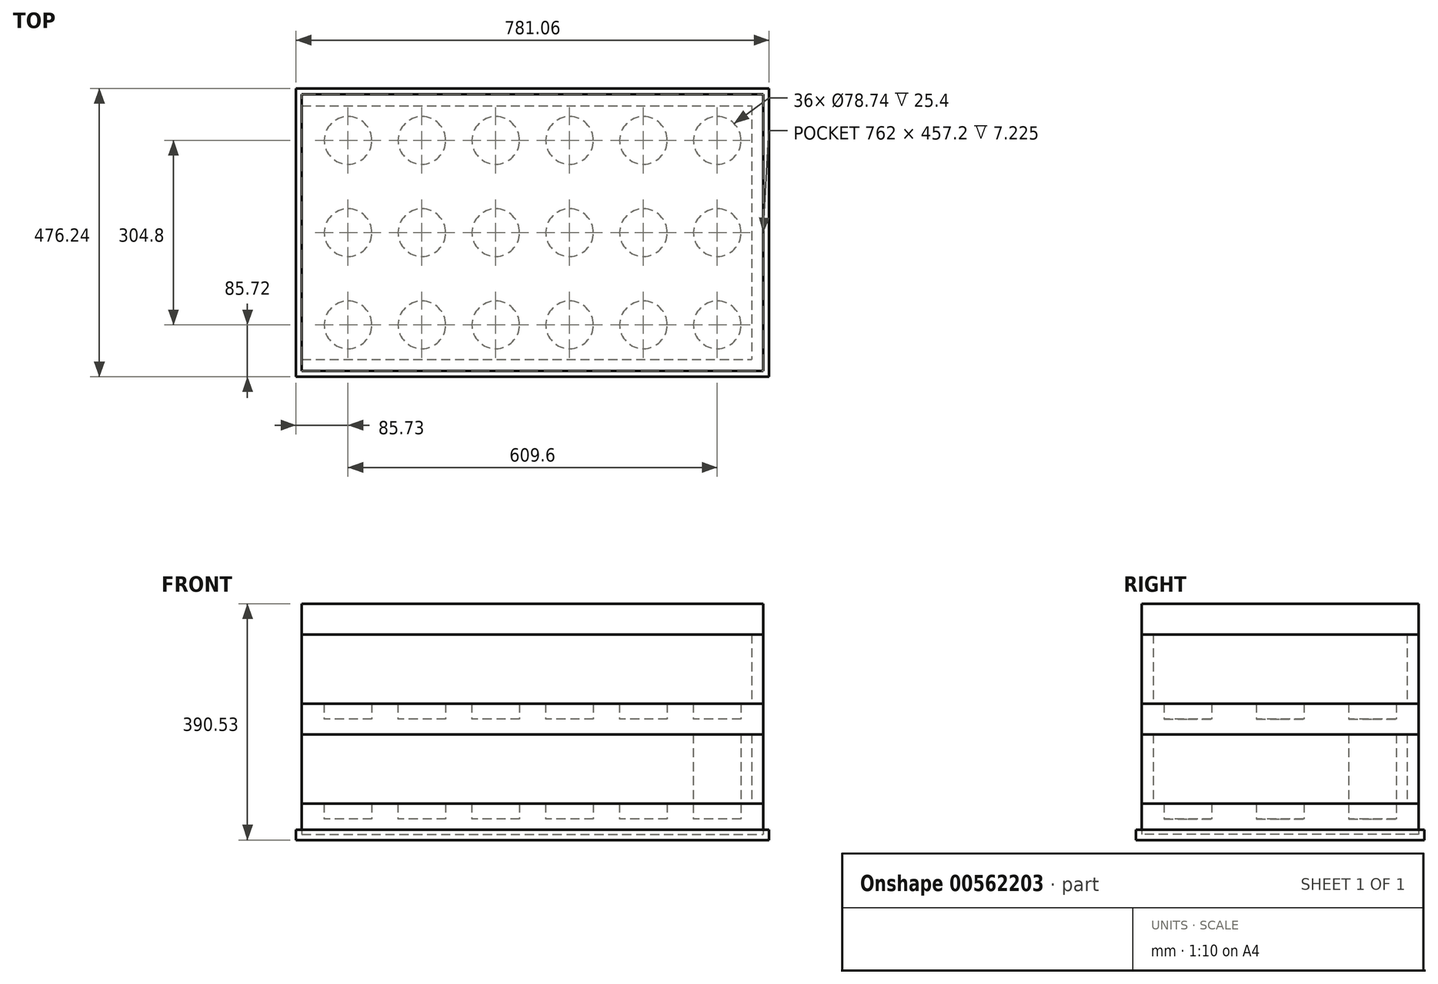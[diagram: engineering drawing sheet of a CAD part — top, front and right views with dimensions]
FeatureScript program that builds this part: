
annotation { "Feature Type Name" : "Feature", "Feature Type Description" : "" }
export const myFeature = defineFeature(function(context is Context, id is Id, definition is map)
    precondition{}
    {
        {
            var Q0;
            Q0=qCreatedBy(makeId("Top.planeOp"),FACE);
            var sketch = newSketch(context, id + "F0", { "sketchPlane" : qUnion([Q0])});
            skLineSegment(sketch, "E0.bottom", {"start": v(-390.53, 238.13) * mm, "end": v(390.53, 238.13) * mm});
            skLineSegment(sketch, "E0.top", {"start": v(-390.53, -238.13) * mm, "end": v(390.53, -238.13) * mm});
            skLineSegment(sketch, "E0.left", {"start": v(-390.53, 238.13) * mm, "end": v(-390.53, -238.13) * mm});
            skLineSegment(sketch, "E0.right", {"start": v(390.53, 238.13) * mm, "end": v(390.52, -238.12) * mm});
            skLineSegment(sketch, "E1", {"start": v(-390.53, 0) * mm, "end": v(390.53, 0) * mm, "construction": true});
            skLineSegment(sketch, "E2", {"start": v(0, -238.13) * mm, "end": v(0, 238.13) * mm, "construction": true});
            skSolve(sketch);
        }
        {
            var Q0;
            Q0=makeQuery(id+"F0.imprint","IMPRINT",FACE,{"disambiguationData":[TD([[makeQuery(id+"F0.imprint","IMPRINT",EDGE,{"derivedFrom":sQuery(id+"F0.wireOp",EDGE,"E0.bottom")}),-1.0]])]});
            extrude(context, id + "F1", {"entities" : qUnion([Q0]), "depth" : (16 + (3 / 8) * 2) * mm, "offsetDistance" : 25.4 * mm});
        }
        {
            var Q0;
            Q0=makeQuery(id+"F1.opExtrude","CAP_FACE",FACE,{"disambiguationData":[OSD([sQuery(id+"F0.wireOp",EDGE,"E0.bottom"),sQuery(id+"F0.wireOp",EDGE,"E0.top"),sQuery(id+"F0.wireOp",EDGE,"E0.left"),sQuery(id+"F0.wireOp",EDGE,"E0.right")])],"isStart":false});
            shell(context, id + "F2", {"entities" : qUnion([Q0]), "thickness" : 9.52 * mm});
        }
        {
            var Q0;
            Q0=makeQuery(id+"F2.opShell","OFFSET_FACE",FACE,{"disambiguationData":[OSD([sQuery(id+"F0.wireOp",EDGE,"E0.bottom"),sQuery(id+"F0.wireOp",EDGE,"E0.top"),sQuery(id+"F0.wireOp",EDGE,"E0.left"),sQuery(id+"F0.wireOp",EDGE,"E0.right")])]});
            var sketch = newSketch(context, id + "F3", { "sketchPlane" : qUnion([Q0])});
            skLineSegment(sketch, "E3.bottom", {"start": v(381, 228.6) * mm, "end": v(-381, 228.6) * mm});
            skLineSegment(sketch, "E3.top", {"start": v(381, -228.6) * mm, "end": v(-381, -228.6) * mm});
            skLineSegment(sketch, "E3.left", {"start": v(381, 228.6) * mm, "end": v(381, -228.6) * mm});
            skLineSegment(sketch, "E3.right", {"start": v(-381, 228.6) * mm, "end": v(-381, -228.6) * mm});
            skSolve(sketch);
        }
        {
            var Q0;
            Q0=makeQuery(id+"F3.imprint","IMPRINT",FACE,{"disambiguationData":[TD([[makeQuery(id+"F3.imprint","IMPRINT",EDGE,{"derivedFrom":sQuery(id+"F3.wireOp",EDGE,"E3.bottom")}),-1.0]])]});
            extrude(context, id + "F4", {"entities" : qUnion([Q0]), "depth" : 25.4 * mm, "offsetDistance" : 25.4 * mm});
        }
        {
            var Q0;
            Q0=makeQuery(id+"F4.opExtrude","CAP_FACE",FACE,{"disambiguationData":[OSD([sQuery(id+"F3.wireOp",EDGE,"E3.bottom"),sQuery(id+"F3.wireOp",EDGE,"E3.top"),sQuery(id+"F3.wireOp",EDGE,"E3.left"),sQuery(id+"F3.wireOp",EDGE,"E3.right")])],"isStart":false});
            var sketch = newSketch(context, id + "F5", { "sketchPlane" : qUnion([Q0])});
            skCircle(sketch, "E4", {"center": v(304.8, 152.4) * mm, "radius": 39.37 * mm});
            skCircle(sketch, "E5.0.1.0", {"center": v(304.8, 0) * mm, "radius": 39.37 * mm});
            skCircle(sketch, "E5.0.2.0", {"center": v(304.8, -152.4) * mm, "radius": 39.37 * mm});
            skCircle(sketch, "E5.1.0.0", {"center": v(182.88, 152.4) * mm, "radius": 39.37 * mm});
            skCircle(sketch, "E5.1.1.0", {"center": v(182.88, 0) * mm, "radius": 39.37 * mm});
            skCircle(sketch, "E5.1.2.0", {"center": v(182.88, -152.4) * mm, "radius": 39.37 * mm});
            skCircle(sketch, "E5.2.0.0", {"center": v(60.96, 152.4) * mm, "radius": 39.37 * mm});
            skCircle(sketch, "E5.2.1.0", {"center": v(60.96, 0) * mm, "radius": 39.37 * mm});
            skCircle(sketch, "E5.2.2.0", {"center": v(60.96, -152.4) * mm, "radius": 39.37 * mm});
            skCircle(sketch, "E5.3.0.0", {"center": v(-60.96, 152.4) * mm, "radius": 39.37 * mm});
            skCircle(sketch, "E5.3.1.0", {"center": v(-60.96, 0) * mm, "radius": 39.37 * mm});
            skCircle(sketch, "E5.3.2.0", {"center": v(-60.96, -152.4) * mm, "radius": 39.37 * mm});
            skCircle(sketch, "E5.4.0.0", {"center": v(-182.88, 152.4) * mm, "radius": 39.37 * mm});
            skCircle(sketch, "E5.4.1.0", {"center": v(-182.88, 0) * mm, "radius": 39.37 * mm});
            skCircle(sketch, "E5.4.2.0", {"center": v(-182.88, -152.4) * mm, "radius": 39.37 * mm});
            skCircle(sketch, "E5.5.0.0", {"center": v(-304.8, 152.4) * mm, "radius": 39.37 * mm});
            skCircle(sketch, "E5.5.1.0", {"center": v(-304.8, 0) * mm, "radius": 39.37 * mm});
            skCircle(sketch, "E5.5.2.0", {"center": v(-304.8, -152.4) * mm, "radius": 39.37 * mm});
            skLineSegment(sketch, "E5.direction1", {"start": v(304.8, 152.4) * mm, "end": v(182.88, 152.4) * mm, "construction": true});
            skLineSegment(sketch, "E5.direction2", {"start": v(304.8, 152.4) * mm, "end": v(304.8, 0) * mm, "construction": true});
            skSolve(sketch);
        }
        {
            var Q0;
            Q0=makeQuery(id+"F5.imprint","IMPRINT",FACE,{"disambiguationData":[TD([[makeQuery(id+"F5.imprint","IMPRINT",EDGE,{"derivedFrom":sQuery(id+"F5.wireOp",EDGE,"E4")}),-1.0]])]});
            extrude(context, id + "F6", {"entities" : qUnion([Q0]), "operationType" : NewBodyOperationType.ADD, "depth" : 25.4 * mm, "offsetDistance" : 25.4 * mm});
        }
        {
            var Q0;
            Q0=makeQuery(id+"F6.boolean.opBoolean","SPLIT",FACE,{"disambiguationData":[TD([makeQuery(id+"F6.opExtrude","SWEPT_FACE",FACE,{"disambiguationData":[OSD([sQuery(id+"F5.wireOp",EDGE,"E4")])]})])],"derivedFrom":makeQuery(id+"F4.opExtrude","CAP_FACE",FACE,{"disambiguationData":[OSD([sQuery(id+"F3.wireOp",EDGE,"E3.bottom"),sQuery(id+"F3.wireOp",EDGE,"E3.top"),sQuery(id+"F3.wireOp",EDGE,"E3.left"),sQuery(id+"F3.wireOp",EDGE,"E3.right")])],"isStart":false})});
            extrude(context, id + "F7", {"entities" : qUnion([Q0]), "depth" : 139.7 * mm, "offsetDistance" : 25.4 * mm});
        }
        {
            var Q0;
            Q0=makeQuery(id+"F6.opExtrude","CAP_FACE",FACE,{"disambiguationData":[OSD([sQuery(id+"F3.wireOp",EDGE,"E3.bottom"),sQuery(id+"F3.wireOp",EDGE,"E3.top"),sQuery(id+"F3.wireOp",EDGE,"E3.left"),sQuery(id+"F3.wireOp",EDGE,"E3.right"),sQuery(id+"F5.wireOp",EDGE,"E4"),sQuery(id+"F5.wireOp",EDGE,"E5.0.1.0"),sQuery(id+"F5.wireOp",EDGE,"E5.0.2.0"),sQuery(id+"F5.wireOp",EDGE,"E5.1.0.0"),sQuery(id+"F5.wireOp",EDGE,"E5.1.1.0"),sQuery(id+"F5.wireOp",EDGE,"E5.1.2.0"),sQuery(id+"F5.wireOp",EDGE,"E5.2.0.0"),sQuery(id+"F5.wireOp",EDGE,"E5.2.1.0"),sQuery(id+"F5.wireOp",EDGE,"E5.2.2.0"),sQuery(id+"F5.wireOp",EDGE,"E5.3.0.0"),sQuery(id+"F5.wireOp",EDGE,"E5.3.1.0"),sQuery(id+"F5.wireOp",EDGE,"E5.3.2.0"),sQuery(id+"F5.wireOp",EDGE,"E5.4.0.0"),sQuery(id+"F5.wireOp",EDGE,"E5.4.1.0"),sQuery(id+"F5.wireOp",EDGE,"E5.4.2.0"),sQuery(id+"F5.wireOp",EDGE,"E5.5.0.0"),sQuery(id+"F5.wireOp",EDGE,"E5.5.1.0"),sQuery(id+"F5.wireOp",EDGE,"E5.5.2.0")])],"isStart":false});
            var sketch = newSketch(context, id + "F8", { "sketchPlane" : qUnion([Q0])});
            skLineSegment(sketch, "E6.bottom", {"start": v(-381, 228.6) * mm, "end": v(381, 228.6) * mm});
            skLineSegment(sketch, "E6.top", {"start": v(-381, 209.55) * mm, "end": v(381, 209.55) * mm});
            skLineSegment(sketch, "E6.left", {"start": v(-381, 228.6) * mm, "end": v(-381, 209.55) * mm});
            skLineSegment(sketch, "E6.right", {"start": v(381, 228.6) * mm, "end": v(381, 209.55) * mm});
            skLineSegment(sketch, "E7.MirrorCS", {"start": v(-381, -209.55) * mm, "end": v(381, -209.55) * mm});
            skLineSegment(sketch, "E8.MirrorCS", {"start": v(-381, -228.6) * mm, "end": v(-381, -209.55) * mm});
            skLineSegment(sketch, "E9.MirrorCS", {"start": v(-381, -228.6) * mm, "end": v(381, -228.6) * mm});
            skLineSegment(sketch, "E10.MirrorCS", {"start": v(381, -228.6) * mm, "end": v(381, -209.55) * mm});
            skLineSegment(sketch, "E11.bottom", {"start": v(-381, 209.55) * mm, "end": v(-361.95, 209.55) * mm});
            skLineSegment(sketch, "E11.top", {"start": v(-381, -209.55) * mm, "end": v(-361.95, -209.55) * mm});
            skLineSegment(sketch, "E11.left", {"start": v(-381, 209.55) * mm, "end": v(-381, -209.55) * mm});
            skLineSegment(sketch, "E11.right", {"start": v(-361.95, 209.55) * mm, "end": v(-361.95, -209.55) * mm});
            skLineSegment(sketch, "E12.MirrorCS", {"start": v(361.95, 209.55) * mm, "end": v(361.95, -209.55) * mm});
            skLineSegment(sketch, "E13.MirrorCS", {"start": v(381, 209.55) * mm, "end": v(381, -209.55) * mm});
            skSolve(sketch);
        }
        {
            var Q0;
            Q0=makeQuery(id+"F8.imprint","IMPRINT",FACE,{"disambiguationData":[TD([[makeQuery(id+"F8.imprint","IMPRINT",EDGE,{"derivedFrom":sQuery(id+"F8.wireOp",EDGE,"E6.bottom")}),-1.0]])]});
            var Q1;
            {var subQ2=sQuery(id+"F8.wireOp",EDGE,"E12.MirrorCS");Q1=makeQuery(id+"F8.imprint","IMPRINT",FACE,{"disambiguationData":[TD([[makeQuery(id+"F8.imprint","IMPRINT",EDGE,{"derivedFrom":subQ2}),1.0]])]});}
            var Q2;
            Q2=makeQuery(id+"F8.imprint","IMPRINT",FACE,{"disambiguationData":[TD([[makeQuery(id+"F8.imprint","IMPRINT",EDGE,{"derivedFrom":sQuery(id+"F8.wireOp",EDGE,"E11.bottom")}),-1.0]])]});
            var Q3;
            Q3=makeQuery(id+"F8.imprint","IMPRINT",FACE,{"disambiguationData":[TD([[makeQuery(id+"F8.imprint","IMPRINT",EDGE,{"derivedFrom":sQuery(id+"F8.wireOp",EDGE,"E8.MirrorCS")}),1.0]])]});
            var Q4;
            Q4=makeQuery(id+"F7.opExtrude","CAP_FACE",FACE,{"disambiguationData":[OSD([sQuery(id+"F3.wireOp",EDGE,"E3.bottom"),sQuery(id+"F3.wireOp",EDGE,"E3.top"),sQuery(id+"F3.wireOp",EDGE,"E3.left"),sQuery(id+"F3.wireOp",EDGE,"E3.right")])],"isStart":false});
            extrude(context, id + "F9", {"entities" : qUnion([Q0, Q1, Q2, Q3]), "endBound" : BoundingType.UP_TO_SURFACE, "depth" : 25.4 * mm, "endBoundEntityFace" : qUnion([Q4]), "offsetDistance" : 25.4 * mm});
        }
        {
            var Q0;
            Q0=makeQuery(id+"F4.opExtrude","SWEPT_BODY",BODY,{"disambiguationData":[OSD([sQuery(id+"F3.wireOp",EDGE,"E3.bottom"),sQuery(id+"F3.wireOp",EDGE,"E3.top"),sQuery(id+"F3.wireOp",EDGE,"E3.left"),sQuery(id+"F3.wireOp",EDGE,"E3.right")])]});
            var Q1;
            Q1=makeQuery(id+"F9.opExtrude","SWEPT_EDGE",EDGE,{"disambiguationData":[OSD([sQuery(id+"F8.wireOp",EDGE,"E6.top"),sQuery(id+"F8.wireOp",EDGE,"E11.bottom"),sQuery(id+"F8.wireOp",EDGE,"E11.right")])]});
            transform(context, id + "F10", {"entities" : qUnion([Q0]), "transformType" : TransformType.TRANSLATION_DISTANCE, "transformDirection" : qUnion([Q1]), "distance" : 165.1 * mm, "oppositeDirection" : true, "makeCopy" : true});
        }
        {
            var Q0;
            Q0=makeQuery(id+"F9.opExtrude","SWEPT_BODY",BODY,{"disambiguationData":[OSD([sQuery(id+"F8.wireOp",EDGE,"E6.bottom"),sQuery(id+"F8.wireOp",EDGE,"E6.top"),sQuery(id+"F8.wireOp",EDGE,"E6.left"),sQuery(id+"F8.wireOp",EDGE,"E6.right"),sQuery(id+"F8.wireOp",EDGE,"E7.MirrorCS"),sQuery(id+"F8.wireOp",EDGE,"E8.MirrorCS"),sQuery(id+"F8.wireOp",EDGE,"E9.MirrorCS"),sQuery(id+"F8.wireOp",EDGE,"E10.MirrorCS"),sQuery(id+"F8.wireOp",EDGE,"E11.left"),sQuery(id+"F8.wireOp",EDGE,"E11.right"),sQuery(id+"F8.wireOp",EDGE,"E12.MirrorCS"),sQuery(id+"F8.wireOp",EDGE,"E13.MirrorCS")])]});
            var Q1;
            Q1=makeQuery(id+"F2.opShell","OFFSET_EDGE",EDGE,{"disambiguationData":[OSD([sQuery(id+"F0.wireOp",EDGE,"E0.bottom"),sQuery(id+"F0.wireOp",EDGE,"E0.left")])]});
            transform(context, id + "F11", {"entities" : qUnion([Q0]), "transformType" : TransformType.TRANSLATION_DISTANCE, "transformDirection" : qUnion([Q1]), "distance" : 165.1 * mm, "oppositeDirection" : true, "makeCopy" : true});
        }
        {
            var Q0;
            Q0=makeQuery(id+"F11.opPattern","COPY",FACE,{"derivedFrom":makeQuery(id+"F9.opExtrude","CAP_FACE",FACE,{"disambiguationData":[OSD([sQuery(id+"F8.wireOp",EDGE,"E6.bottom"),sQuery(id+"F8.wireOp",EDGE,"E6.top"),sQuery(id+"F8.wireOp",EDGE,"E6.left"),sQuery(id+"F8.wireOp",EDGE,"E6.right"),sQuery(id+"F8.wireOp",EDGE,"E7.MirrorCS"),sQuery(id+"F8.wireOp",EDGE,"E8.MirrorCS"),sQuery(id+"F8.wireOp",EDGE,"E9.MirrorCS"),sQuery(id+"F8.wireOp",EDGE,"E10.MirrorCS"),sQuery(id+"F8.wireOp",EDGE,"E11.left"),sQuery(id+"F8.wireOp",EDGE,"E11.right"),sQuery(id+"F8.wireOp",EDGE,"E12.MirrorCS"),sQuery(id+"F8.wireOp",EDGE,"E13.MirrorCS")])],"isStart":false}),"instanceName":"1"});
            var sketch = newSketch(context, id + "F12", { "sketchPlane" : qUnion([Q0])});
            skLineSegment(sketch, "E14.bottom", {"start": v(-381, 228.6) * mm, "end": v(381, 228.6) * mm});
            skLineSegment(sketch, "E14.top", {"start": v(-381, -228.6) * mm, "end": v(381, -228.6) * mm});
            skLineSegment(sketch, "E14.left", {"start": v(-381, 228.6) * mm, "end": v(-381, -228.6) * mm});
            skLineSegment(sketch, "E14.right", {"start": v(381, 228.6) * mm, "end": v(381, -228.6) * mm});
            skSolve(sketch);
        }
        {
            var Q0;
            Q0 = qSketchRegion(id + "F12", true);
            extrude(context, id + "F13", {"entities" : qUnion([Q0]), "depth" : 50.8 * mm, "offsetDistance" : 25.4 * mm});
        }
    });
